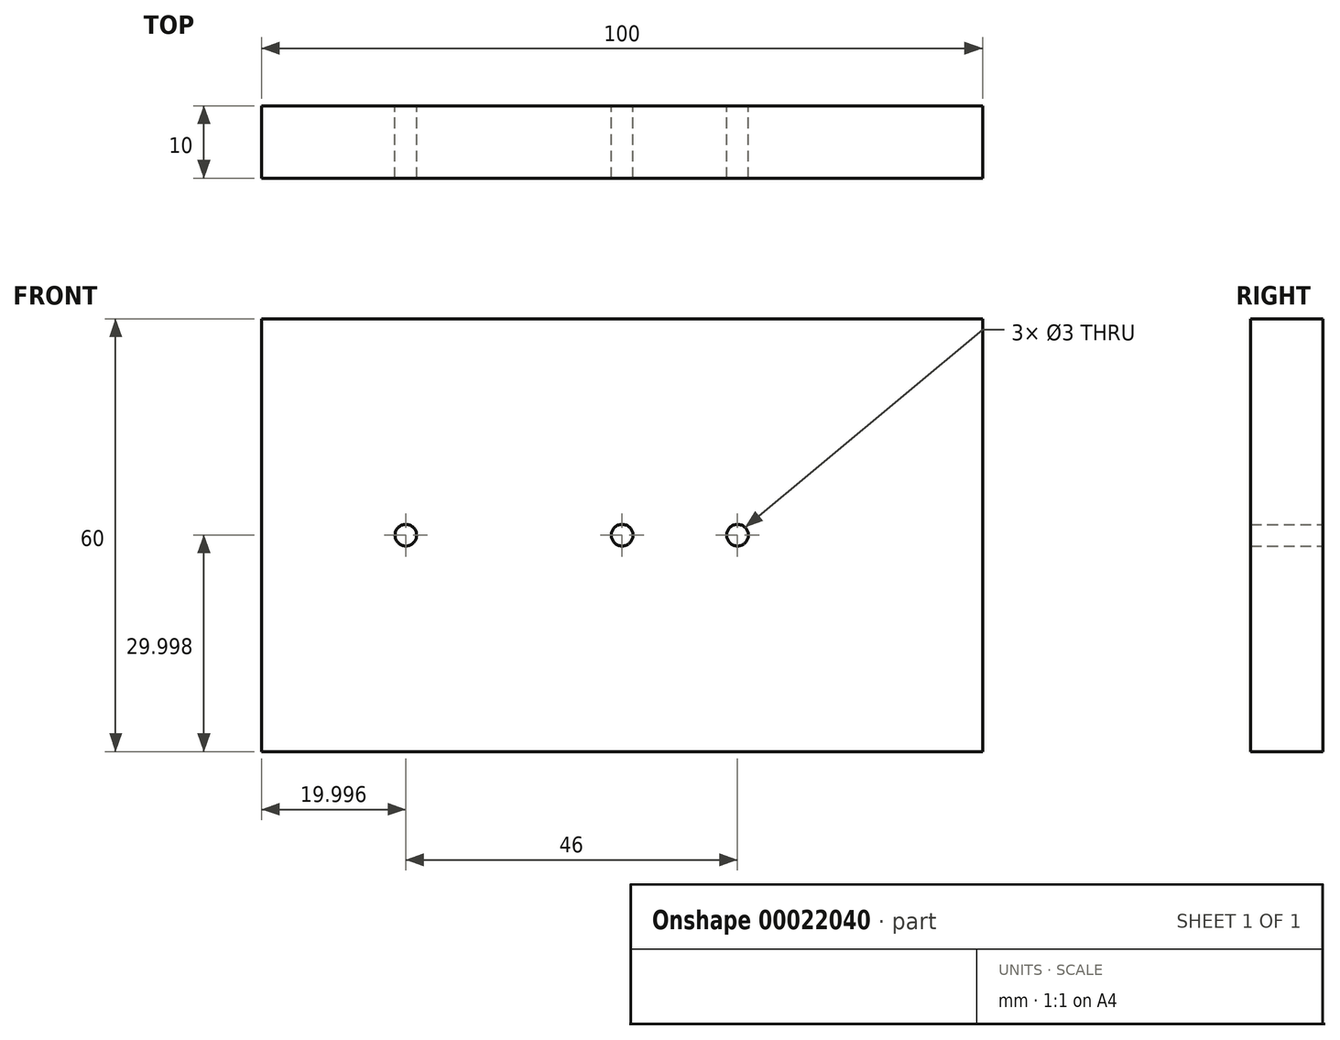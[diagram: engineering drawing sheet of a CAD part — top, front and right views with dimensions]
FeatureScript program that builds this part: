
annotation { "Feature Type Name" : "Feature", "Feature Type Description" : "" }
export const myFeature = defineFeature(function(context is Context, id is Id, definition is map)
    precondition{}
    {
        {
            var Q0;
            Q0=qCreatedBy(makeId("Front.planeOp"),FACE);
            var sketch = newSketch(context, id + "F0", { "sketchPlane" : qUnion([Q0])});
            skLineSegment(sketch, "E0.bottom", {"start": v(-42.91, 34.16) * mm, "end": v(57.09, 34.16) * mm});
            skLineSegment(sketch, "E0.top", {"start": v(-42.91, -25.84) * mm, "end": v(57.09, -25.84) * mm});
            skLineSegment(sketch, "E0.left", {"start": v(-42.91, 34.16) * mm, "end": v(-42.91, -25.84) * mm});
            skLineSegment(sketch, "E0.right", {"start": v(57.09, 34.16) * mm, "end": v(57.09, -25.84) * mm});
            skLineSegment(sketch, "E1", {"start": v(-42.91, 4.16) * mm, "end": v(57.09, 4.16) * mm});
            skCircle(sketch, "E2", {"center": v(-22.91, 4.16) * mm, "radius": 1.5 * mm});
            skCircle(sketch, "E3", {"center": v(7.09, 4.16) * mm, "radius": 1.5 * mm});
            skCircle(sketch, "E4", {"center": v(23.09, 4.16) * mm, "radius": 1.5 * mm});
            skSolve(sketch);
        }
        {
            var Q0;
            {var subQ14=sQuery(id+"F0.wireOp",EDGE,"E0.bottom");Q0=makeQuery(id+"F0.imprint","IMPRINT",FACE,{"disambiguationData":[TD([[makeQuery(id+"F0.imprint","IMPRINT",EDGE,{"derivedFrom":subQ14}),-1.0]])]});}
            var Q1;
            {var subQ14=sQuery(id+"F0.wireOp",EDGE,"E0.top");Q1=makeQuery(id+"F0.imprint","IMPRINT",FACE,{"disambiguationData":[TD([[makeQuery(id+"F0.imprint","IMPRINT",EDGE,{"derivedFrom":subQ14}),1.0]])]});}
            extrude(context, id + "F1", {"entities" : qUnion([Q0, Q1]), "depth" : 10 * mm});
        }
    });
